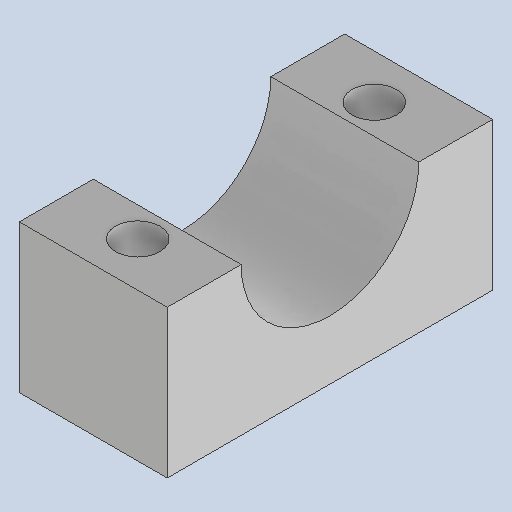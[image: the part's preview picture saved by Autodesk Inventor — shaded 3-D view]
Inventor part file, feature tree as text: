
AUTODESK INVENTOR PART (.ipt)
format: ipt  version: 2025.1 (Build 291241000, 241)  size: 110,592 bytes
history: native  units: mm
features: other x3, sketch x2
ambient origin geometry x8: Origin, YZ Plane, XZ Plane, XY Plane, X Axis, Y Axis, Z Axis, Center Point
bodies: Solid1 (feature_tree)
feature tree (5):
  other  "145 part.ipt"
  other  "Solid1::145 part.ipt"
  other  "TaggingFeature1"
  sketch  "Sketch1"  dims[d0=10.0mm]
  sketch  "Sketch2"
